# Revit family: Vuelift_Round_Acrylic-3_Story
name_source: partatom
category: Generic Models
units: mm (PartAtom-declared; Revit-internal decimal feet)

## family parameters
Always vertical = Yes
Can host rebar = No
Classification Number = 23.50.05.14
Cut with Voids When Loaded = No
Maintain Annotation Orientation = No
Part Type = Normal
Room Calculation Point = No
Round Connector Dimension = Use Diameter
Shared = No
Work Plane-Based = No

## types (2) — shared parameters
Applied Code = ASME 17.1-2016 SEC. 5.3 NEC 2008
Cabinet Floor Area = 11.91 Square Feet  [1.11 sq.meters]
Cabinet Interior Height = 84 Inches   [2133 mm]
Cabinet Weight = 700 lbs.  [318kg]
Capacity = 840 lbs.  [381] kg]
Classification = Residential Building
Default Elevation = 0"
Elevator Height = 84"
Glass = Glass
Hoistway Door = 84"
Load = 0 VA
Manufacturer = savaria
Model = Round Acrylic
Number of Floors = 3
Poles = 1
Power Supply = 50/60Hz Single Phase 230V
URL = https://www.savaria.com
Voltge_x = 0 V
Walls = Full Clear Acrylic-Compiles with ANSI Z97.1

## per-type parameters (varying)
| type | Frame |
| Vuelift Round Acrylic - S- White Sandtex | Powder Coat - Savaria - White Sandtex |
| Vuelift Round Acrylic - S- Black Sandtex | Powder Coat - Savaria - Black Sandtex |

## geometry (parser evidence)
native form markers: Sweep x10
no freeform markers — native parametric forms only
